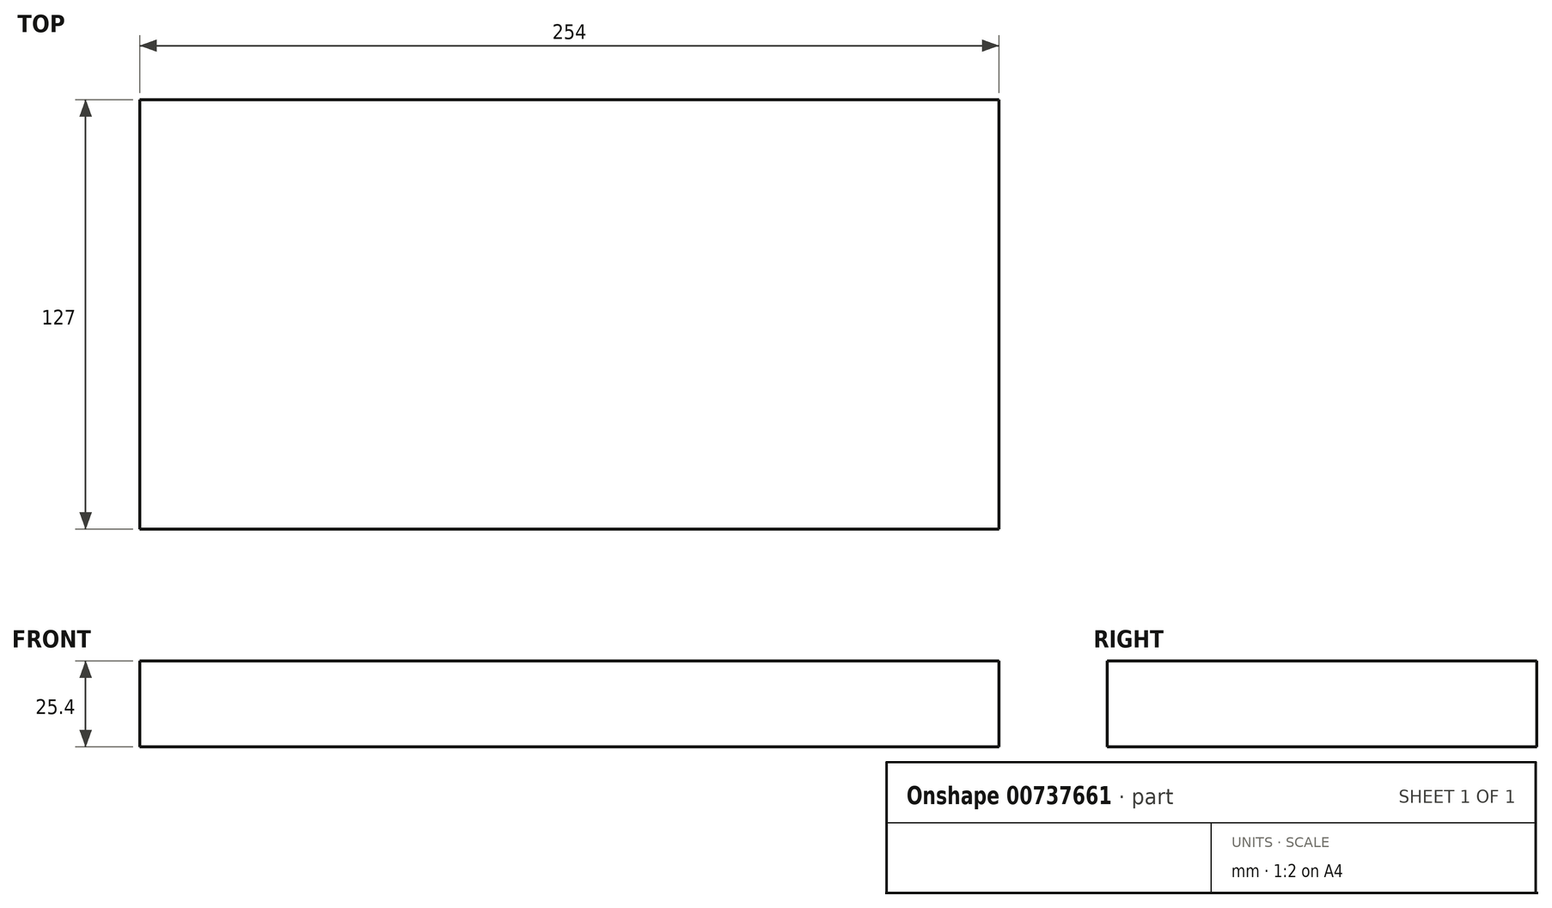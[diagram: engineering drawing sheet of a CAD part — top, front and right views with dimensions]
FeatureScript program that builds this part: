
annotation { "Feature Type Name" : "Feature", "Feature Type Description" : "" }
export const myFeature = defineFeature(function(context is Context, id is Id, definition is map)
    precondition{}
    {
        {
            var Q0;
            Q0=qCreatedBy(makeId("Top.planeOp"),FACE);
            var sketch = newSketch(context, id + "F0", { "sketchPlane" : qUnion([Q0])});
            skLineSegment(sketch, "E0.bottom", {"start": v(0, 0) * mm, "end": v(254, 0) * mm});
            skLineSegment(sketch, "E0.top", {"start": v(0, 127) * mm, "end": v(254, 127) * mm});
            skLineSegment(sketch, "E0.left", {"start": v(0, 0) * mm, "end": v(0, 127) * mm});
            skLineSegment(sketch, "E0.right", {"start": v(254, 0) * mm, "end": v(254, 127) * mm});
            skSolve(sketch);
        }
        {
            var Q0;
            Q0=makeQuery(id+"F0.imprint","IMPRINT",FACE,{"disambiguationData":[TD([[makeQuery(id+"F0.imprint","IMPRINT",EDGE,{"derivedFrom":sQuery(id+"F0.wireOp",EDGE,"E0.bottom")}),1.0]])]});
            extrude(context, id + "F1", {"entities" : qUnion([Q0]), "depth" : 25.4 * mm, "offsetDistance" : 25.4 * mm});
        }
    });
